# Revit family: xxHand_Washing_Station-Portable-Acorn_Engineering-Deluxe_Portable_Wash_Ware-PS10XX_Series
name_source: partatom
category: Plumbing Fixtures
units: mm (PartAtom-declared; Revit-internal decimal feet)

## family parameters
Always vertical = No
Cut with Voids When Loaded = No
OmniClass Number = 23.45.05.14.14
OmniClass Title = Sinks/Lavatories
Part Type = Normal
Room Calculation Point = No
Round Connector Dimension = Use Diameter
Shared = Yes
Work Plane-Based = Yes

## types (3) — shared parameters
-JR 31” Junior Rim Height = No
ASSE 1069/1070 Certified = Yes
Assembly Code = D2010310
Bowl Depth = 6"
Bowl Length = 9 1/2"
Bowl Shape = Oval
Bowl Width = 14 1/2"
CW Connection = No
Default Elevation = 0"
F/A Height = 0"
Faucet Handle = No
Finish = Stainless Steel-Acorn Engineering-Satin
Finish- Bowl = Stainless Steel-Acorn Engineering-Satin #4
Flow Rate = 0.5 GPM (1.9 LPM)
Gooseneck Faucet = No
HW Connection = No
Height- Counter = 36 3/4"
Length = 16 1/2"
Manufacturer = Aconr Engineering
Material = Stainless Steel-Acorn Engineering-Satin
Meets NSF and Lead-Free Standard = Yes
No -PH3, -TR = Yes
No Gooseneck Faucet = Yes
No Soap Dispenser = Yes
PS1000-5GW 5-Gallon (19 Liter) Wastewater Tank (PS1021, PS1041) = No
PS1000-F11 Gooseneck Spout = No
PS1000-F21 Gooseneck, Wrist Blade Handle = No
PS1000-F31 Gooseneck, Battery Sensor Operated = No
PS1000-F40 Gooseneck, Single Handle = No
PS1000-PH3 3-Bay C-Fold Paper Holder = No
PS1000-PS Pump Soap Dispenser = No
PS1000-SG Wrap Around Splash Guard = No
PS1000-SG1 Wrap Around Splash Guard, 2-Bay Paper Holder and Soap Bottle Holder = No
PS1000-SG2 Wrap Around Splash Guard, 2-Bay Paper Holder = No
PS1000-SSO Sensor Operated Soap Dispenser = No
PS1000-TR 6-Gallon Trash Receptacle = No
PS1015 Hose Supply, Hose Waste = No
PS1020 Hose Supply, Wastewater Tank = No
PS1021 Hose Supply, Wastewater Tank, Flood = No
PS1040 Hose Supply, Water Heater, Wastewater Tank = No
PS1041 Hose Supply, Water Heater, Wastewater Tank, Flood Prevention Feature = No
Portable Sink Water Supply = Self-Contained
Product Documentation Link = https://www.acorneng.com
Product Page URL = https://www.acorneng.com
Soap Dispenser = No
Tempered Water Connection = Yes
URL = https://www.acorneng.com
Vent Connection = No
WH-DECAL 10” Sticky Decal “Wash Your Hands” = No
Waste Connection = Yes
Water Tank Capacity = 5-gallon (19 liter) tank
Width = 25"
zero-valued in all types: CWFU, HWFU, WFU

## per-type parameters (varying)
| type | Description | Indoor/Outdoor Use | PS1000-5GF 5-Gallon (19 Liter) Fresh Water Tank (PS1010, PS1030) | PS1000-6GW 6-Gallon (23 Liter) Wastewater Tank (PS1010, PS1020, PS1030, PS1040) | Power Supply | UL Listed Mini Tank Water Heater |
| PS1010 | Foot Pump - Portable Wash-Ware® Hand Washing Station | Suitable for Outdoor Use | Yes | Yes |  | No |
| PS1030 | On-Demand Pump - Portable Wash-Ware® Hand Washing Station | Indoor Use Only | Yes | Yes | 110VAC Plug-in, On-Demand Pump | No |
| PS1042 | On-Demand Pump, Water Heater, Fresh Tank, Waste Hose Deluxe Portable Wash-Ware® Hand Wash | Indoor Use Only | No | No | 110-120VAC, 15 Amp Receptacle | Yes |

note: column(s) folded — value = type name in every type: Model

## geometry (parser evidence)
native form markers: Sweep x3
no freeform markers — native parametric forms only
